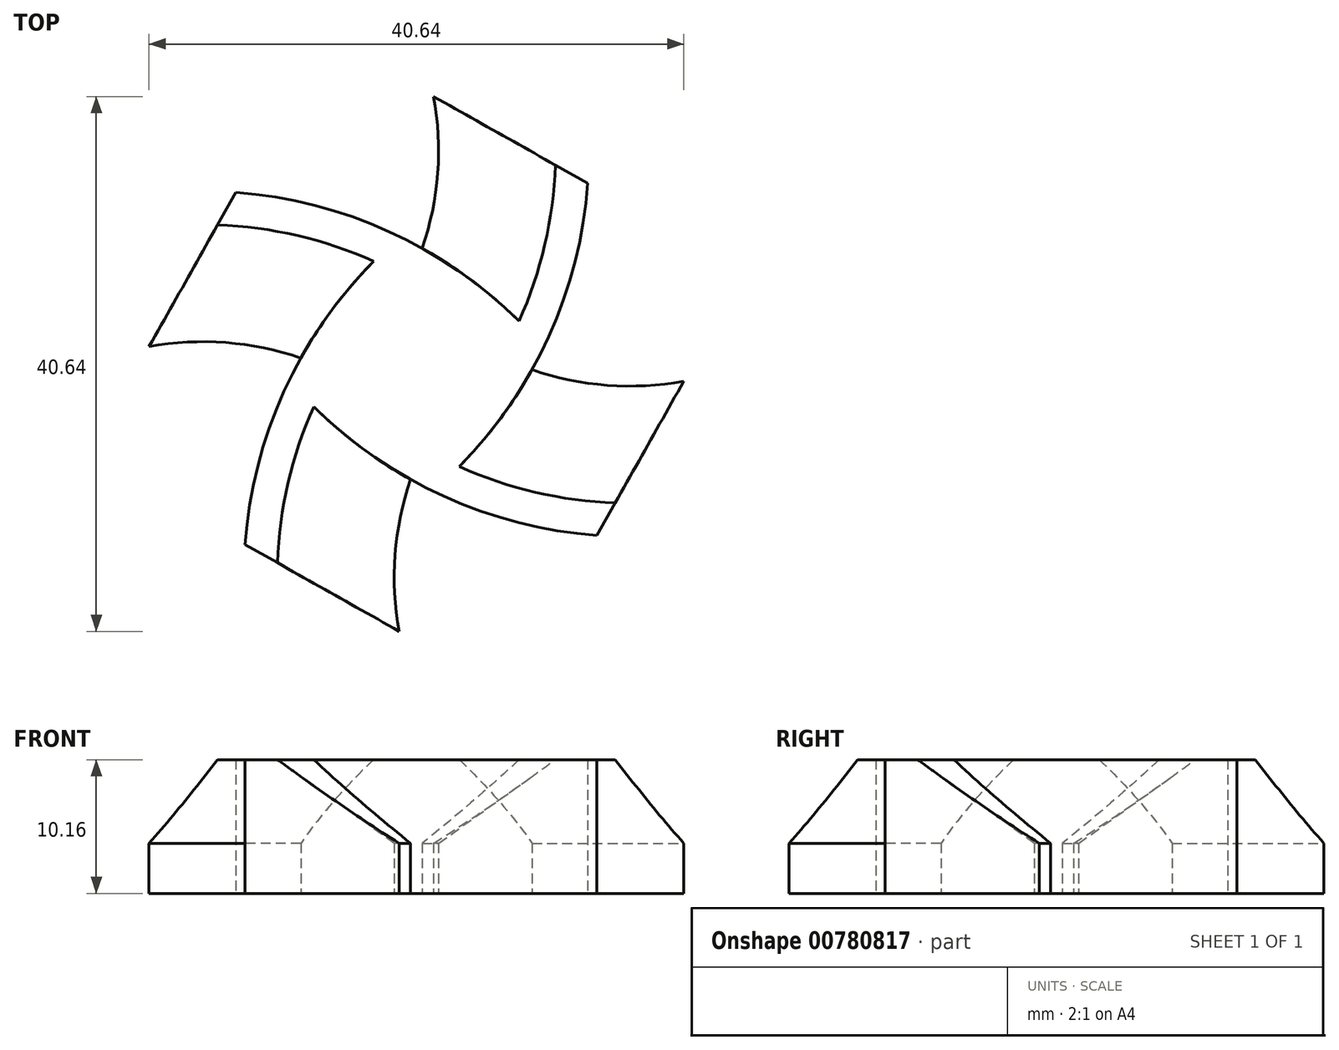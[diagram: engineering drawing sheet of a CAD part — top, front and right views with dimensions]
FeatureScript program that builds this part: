
annotation { "Feature Type Name" : "Feature", "Feature Type Description" : "" }
export const myFeature = defineFeature(function(context is Context, id is Id, definition is map)
    precondition{}
    {
        {
            var Q0;
            Q0=qCreatedBy(makeId("Top.planeOp"),FACE);
            var sketch = newSketch(context, id + "F0", { "sketchPlane" : qUnion([Q0])});
            skCircle(sketch, "E0", {"center": v(0, 0) * mm, "radius": 7.62 * mm});
            skArc(sketch, "E1", {"start": v(0, 7.62) * mm, "mid": v(1.57, 13.88) * mm, "end": v(1.3, 20.32) * mm});
            skArc(sketch, "E2.0", {"start": v(6.45, -4.06) * mm, "mid": v(11, 4.36) * mm, "end": v(13.02, 13.72) * mm});
            skLineSegment(sketch, "E3", {"start": v(1.3, 20.32) * mm, "end": v(13.02, 13.72) * mm});
            skArc(sketch, "E4.1.0", {"start": v(-7.62, 0) * mm, "mid": v(-13.88, 1.57) * mm, "end": v(-20.32, 1.3) * mm});
            skLineSegment(sketch, "E4.1.1", {"start": v(-20.32, 1.3) * mm, "end": v(-13.72, 13.02) * mm});
            skArc(sketch, "E4.1.2", {"start": v(4.06, 6.45) * mm, "mid": v(-4.36, 11) * mm, "end": v(-13.72, 13.02) * mm});
            skArc(sketch, "E4.2.0", {"start": v(0, -7.62) * mm, "mid": v(-1.57, -13.88) * mm, "end": v(-1.3, -20.32) * mm});
            skLineSegment(sketch, "E4.2.1", {"start": v(-1.3, -20.32) * mm, "end": v(-13.02, -13.72) * mm});
            skArc(sketch, "E4.2.2", {"start": v(-6.45, 4.06) * mm, "mid": v(-11, -4.36) * mm, "end": v(-13.02, -13.72) * mm});
            skArc(sketch, "E4.3.0", {"start": v(7.62, 0) * mm, "mid": v(13.88, -1.57) * mm, "end": v(20.32, -1.3) * mm});
            skLineSegment(sketch, "E4.3.1", {"start": v(20.32, -1.3) * mm, "end": v(13.72, -13.02) * mm});
            skArc(sketch, "E4.3.2", {"start": v(-4.06, -6.45) * mm, "mid": v(4.36, -11) * mm, "end": v(13.72, -13.02) * mm});
            skSolve(sketch);
        }
        {
            var Q0;
            Q0=qSketchRegion(id+"F0",true);
            var Q1;
            {var subQ0=sQuery(id+"F0.wireOp",EDGE,"E0");var subQ4=makeQuery(id+"F0.imprint","INTERSECT",VERTEX,{"derivedFrom":[subQ0,sQuery(id+"F0.wireOp",EDGE,"E4.1.2")]});Q1=makeQuery(id+"F0.imprint","IMPRINT",FACE,{"disambiguationData":[TD([[makeQuery(id+"F0.imprint","IMPRINT",EDGE,{"disambiguationData":[TD([[subQ4,1.0]])],"derivedFrom":subQ0}),1.0]])]});}
            extrude(context, id + "F1", {"entities" : qUnion([Q0, Q1]), "depth" : 10.16 * mm, "offsetDistance" : 25.4 * mm});
        }
        {
            var Q0;
            Q0=makeQuery(id+"F1.opExtrude","CAP_EDGE",EDGE,{"disambiguationData":[OSD([sQuery(id+"F0.wireOp",EDGE,"E1")])],"isStart":false});
            var Q1;
            Q1=makeQuery(id+"F1.opExtrude","CAP_EDGE",EDGE,{"disambiguationData":[OSD([sQuery(id+"F0.wireOp",EDGE,"E4.1.0")])],"isStart":false});
            var Q2;
            Q2=makeQuery(id+"F1.opExtrude","CAP_EDGE",EDGE,{"disambiguationData":[OSD([sQuery(id+"F0.wireOp",EDGE,"E4.2.0")])],"isStart":false});
            var Q3;
            Q3=makeQuery(id+"F1.opExtrude","CAP_EDGE",EDGE,{"disambiguationData":[OSD([sQuery(id+"F0.wireOp",EDGE,"E4.3.0")])],"isStart":false});
            chamfer(context, id + "F2", {"entities" : qUnion([Q0, Q1, Q2, Q3]), "chamferType" : ChamferType.TWO_OFFSETS, "width1" : 6.35 * mm, "oppositeDirection" : false, "width2" : 8.9 * mm, "tangentPropagation" : true});
        }
    });
